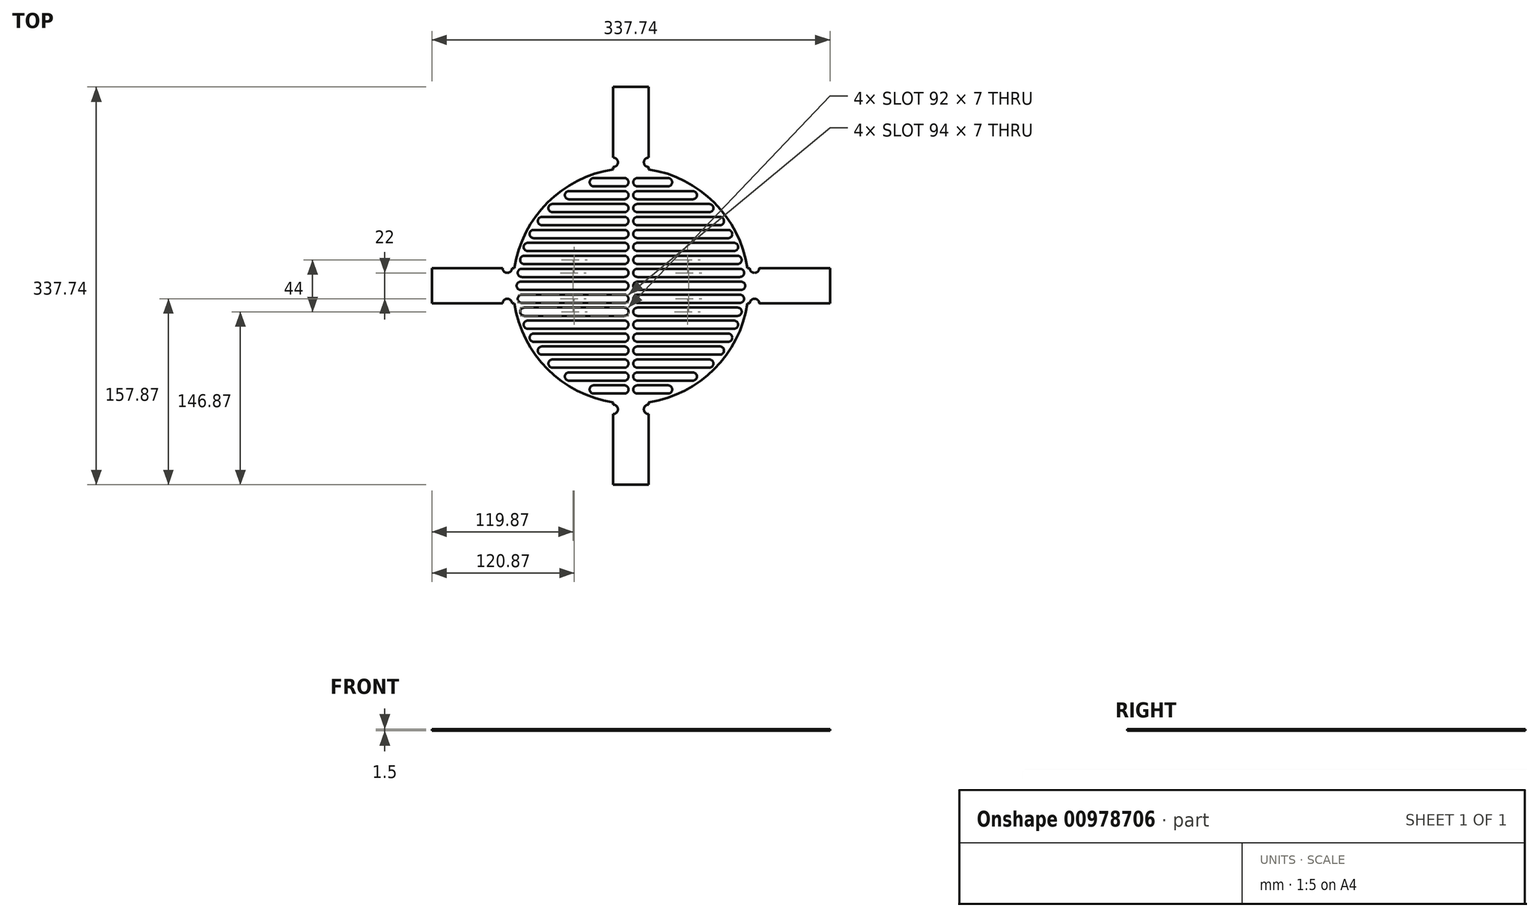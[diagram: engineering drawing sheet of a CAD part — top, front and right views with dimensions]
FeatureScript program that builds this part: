
annotation { "Feature Type Name" : "Feature", "Feature Type Description" : "" }
export const myFeature = defineFeature(function(context is Context, id is Id, definition is map)
    precondition{}
    {
        {
            var Q0;
            Q0=qCreatedBy(makeId("Top.planeOp"),FACE);
            var sketch = newSketch(context, id + "F0", { "sketchPlane" : qUnion([Q0])});
            skCircle(sketch, "E0", {"center": v(0, 0) * mm, "radius": 100 * mm});
            skSolve(sketch);
        }
        {
            var Q0;
            Q0 = qSketchRegion(id + "F0", true);
            extrude(context, id + "F1", {"entities" : qUnion([Q0]), "oppositeDirection" : true, "depth" : 1.5 * mm, "offsetDistance" : 25 * mm});
        }
        {
            var Q0;
            Q0=makeQuery(id+"F0.imprint","IMPRINT",FACE,{"disambiguationData":[TD([[makeQuery(id+"F0.imprint","IMPRINT",EDGE,{"derivedFrom":sQuery(id+"F0.wireOp",EDGE,"E0")}),1.0]])]});
            var sketch = newSketch(context, id + "F2", { "sketchPlane" : qUnion([Q0])});
            skLineSegment(sketch, "E1.bottom", {"start": v(-98.87, 15) * mm, "end": v(-168.87, 15) * mm});
            skLineSegment(sketch, "E1.top", {"start": v(-98.87, -15) * mm, "end": v(-168.87, -15) * mm});
            skLineSegment(sketch, "E1.left", {"start": v(-98.87, 15) * mm, "end": v(-98.87, -15) * mm});
            skLineSegment(sketch, "E1.right", {"start": v(-168.87, 15) * mm, "end": v(-168.87, -15) * mm});
            skLineSegment(sketch, "E2.bottom", {"start": v(98.87, 15) * mm, "end": v(168.87, 15) * mm});
            skLineSegment(sketch, "E2.top", {"start": v(98.87, -15) * mm, "end": v(168.87, -15) * mm});
            skLineSegment(sketch, "E2.left", {"start": v(98.87, 15) * mm, "end": v(98.87, -15) * mm});
            skLineSegment(sketch, "E2.right", {"start": v(168.87, 15) * mm, "end": v(168.87, -15) * mm});
            skLineSegment(sketch, "E3.bottom", {"start": v(-15, 98.87) * mm, "end": v(15, 98.87) * mm});
            skLineSegment(sketch, "E3.top", {"start": v(-15, 168.87) * mm, "end": v(15, 168.87) * mm});
            skLineSegment(sketch, "E3.left", {"start": v(-15, 98.87) * mm, "end": v(-15, 168.87) * mm});
            skLineSegment(sketch, "E3.right", {"start": v(15, 98.87) * mm, "end": v(15, 168.87) * mm});
            skLineSegment(sketch, "E4.bottom", {"start": v(-15, -98.87) * mm, "end": v(15, -98.87) * mm});
            skLineSegment(sketch, "E4.top", {"start": v(-15, -168.87) * mm, "end": v(15, -168.87) * mm});
            skLineSegment(sketch, "E4.left", {"start": v(-15, -98.87) * mm, "end": v(-15, -168.87) * mm});
            skLineSegment(sketch, "E4.right", {"start": v(15, -98.87) * mm, "end": v(15, -168.87) * mm});
            skSolve(sketch);
        }
        {
            var Q0;
            Q0 = qSketchRegion(id + "F2", true);
            extrude(context, id + "F3", {"entities" : qUnion([Q0]), "operationType" : NewBodyOperationType.ADD, "oppositeDirection" : true, "depth" : 1.5 * mm, "offsetDistance" : 25 * mm});
        }
        {
            var Q0;
            Q0=makeQuery(id+"F0.imprint","IMPRINT",FACE,{"disambiguationData":[TD([[makeQuery(id+"F0.imprint","IMPRINT",EDGE,{"derivedFrom":sQuery(id+"F0.wireOp",EDGE,"E0")}),1.0]])]});
            var sketch = newSketch(context, id + "F4", { "sketchPlane" : qUnion([Q0])});
            skLineSegment(sketch, "E5", {"start": v(-5.5, 0) * mm, "end": v(-93.5, 0) * mm});
            skArc(sketch, "E6.0.startCap", {"start": v(-5.5, 3.5) * mm, "mid": v(-2, 0) * mm, "end": v(-5.5, -3.5) * mm});
            skArc(sketch, "E6.0.endCap", {"start": v(-93.5, -3.5) * mm, "mid": v(-97, 0) * mm, "end": v(-93.5, 3.5) * mm});
            skLineSegment(sketch, "E6.0.left", {"start": v(-5.5, -3.5) * mm, "end": v(-93.5, -3.5) * mm});
            skLineSegment(sketch, "E6.0.right", {"start": v(-5.5, 3.5) * mm, "end": v(-93.5, 3.5) * mm});
            skLineSegment(sketch, "E7", {"start": v(-5.5, 11) * mm, "end": v(-92.5, 11) * mm});
            skArc(sketch, "E8.0.startCap", {"start": v(-5.5, 14.5) * mm, "mid": v(-2, 11) * mm, "end": v(-5.5, 7.5) * mm});
            skArc(sketch, "E8.0.endCap", {"start": v(-92.5, 7.5) * mm, "mid": v(-96, 11) * mm, "end": v(-92.5, 14.5) * mm});
            skLineSegment(sketch, "E8.0.left", {"start": v(-5.5, 7.5) * mm, "end": v(-92.5, 7.5) * mm});
            skLineSegment(sketch, "E8.0.right", {"start": v(-5.5, 14.5) * mm, "end": v(-92.5, 14.5) * mm});
            skLineSegment(sketch, "E9", {"start": v(-5.5, 22) * mm, "end": v(-90.5, 22) * mm});
            skArc(sketch, "E10.0.startCap", {"start": v(-5.5, 25.5) * mm, "mid": v(-2, 22) * mm, "end": v(-5.5, 18.5) * mm});
            skArc(sketch, "E10.0.endCap", {"start": v(-90.5, 18.5) * mm, "mid": v(-94, 22) * mm, "end": v(-90.5, 25.5) * mm});
            skLineSegment(sketch, "E10.0.left", {"start": v(-5.5, 18.5) * mm, "end": v(-90.5, 18.5) * mm});
            skLineSegment(sketch, "E10.0.right", {"start": v(-5.5, 25.5) * mm, "end": v(-90.5, 25.5) * mm});
            skLineSegment(sketch, "E11", {"start": v(-5.5, 44) * mm, "end": v(-82.5, 44) * mm});
            skArc(sketch, "E12.0.startCap", {"start": v(-5.5, 47.5) * mm, "mid": v(-2, 44) * mm, "end": v(-5.5, 40.5) * mm});
            skArc(sketch, "E12.0.endCap", {"start": v(-82.5, 40.5) * mm, "mid": v(-86, 44) * mm, "end": v(-82.5, 47.5) * mm});
            skLineSegment(sketch, "E12.0.left", {"start": v(-5.5, 40.5) * mm, "end": v(-82.5, 40.5) * mm});
            skLineSegment(sketch, "E12.0.right", {"start": v(-5.5, 47.5) * mm, "end": v(-82.5, 47.5) * mm});
            skLineSegment(sketch, "E13", {"start": v(-5.5, 33) * mm, "end": v(-87.5, 33) * mm});
            skArc(sketch, "E14.0.startCap", {"start": v(-5.5, 36.5) * mm, "mid": v(-2, 33) * mm, "end": v(-5.5, 29.5) * mm});
            skArc(sketch, "E14.0.endCap", {"start": v(-87.5, 29.5) * mm, "mid": v(-91, 33) * mm, "end": v(-87.5, 36.5) * mm});
            skLineSegment(sketch, "E14.0.left", {"start": v(-5.5, 29.5) * mm, "end": v(-87.5, 29.5) * mm});
            skLineSegment(sketch, "E14.0.right", {"start": v(-5.5, 36.5) * mm, "end": v(-87.5, 36.5) * mm});
            skLineSegment(sketch, "E15", {"start": v(-5.5, 55) * mm, "end": v(-75.5, 55) * mm});
            skArc(sketch, "E16.0.startCap", {"start": v(-5.5, 58.5) * mm, "mid": v(-2, 55) * mm, "end": v(-5.5, 51.5) * mm});
            skArc(sketch, "E16.0.endCap", {"start": v(-75.5, 51.5) * mm, "mid": v(-79, 55) * mm, "end": v(-75.5, 58.5) * mm});
            skLineSegment(sketch, "E16.0.left", {"start": v(-5.5, 51.5) * mm, "end": v(-75.5, 51.5) * mm});
            skLineSegment(sketch, "E16.0.right", {"start": v(-5.5, 58.5) * mm, "end": v(-75.5, 58.5) * mm});
            skLineSegment(sketch, "E17", {"start": v(-5.5, 66) * mm, "end": v(-66.5, 66) * mm});
            skArc(sketch, "E18.0.startCap", {"start": v(-5.5, 69.5) * mm, "mid": v(-2, 66) * mm, "end": v(-5.5, 62.5) * mm});
            skArc(sketch, "E18.0.endCap", {"start": v(-66.5, 62.5) * mm, "mid": v(-70, 66) * mm, "end": v(-66.5, 69.5) * mm});
            skLineSegment(sketch, "E18.0.left", {"start": v(-5.5, 62.5) * mm, "end": v(-66.5, 62.5) * mm});
            skLineSegment(sketch, "E18.0.right", {"start": v(-5.5, 69.5) * mm, "end": v(-66.5, 69.5) * mm});
            skLineSegment(sketch, "E19", {"start": v(-5.5, 77) * mm, "end": v(-52.5, 77) * mm});
            skArc(sketch, "E20.0.startCap", {"start": v(-5.5, 80.5) * mm, "mid": v(-2, 77) * mm, "end": v(-5.5, 73.5) * mm});
            skArc(sketch, "E20.0.endCap", {"start": v(-52.5, 73.5) * mm, "mid": v(-56, 77) * mm, "end": v(-52.5, 80.5) * mm});
            skLineSegment(sketch, "E20.0.left", {"start": v(-5.5, 73.5) * mm, "end": v(-52.5, 73.5) * mm});
            skLineSegment(sketch, "E20.0.right", {"start": v(-5.5, 80.5) * mm, "end": v(-52.5, 80.5) * mm});
            skLineSegment(sketch, "E21", {"start": v(-5.5, 88) * mm, "end": v(-31.5, 88) * mm});
            skArc(sketch, "E22.0.startCap", {"start": v(-5.5, 91.5) * mm, "mid": v(-2, 88) * mm, "end": v(-5.5, 84.5) * mm});
            skArc(sketch, "E22.0.endCap", {"start": v(-31.5, 84.5) * mm, "mid": v(-35, 88) * mm, "end": v(-31.5, 91.5) * mm});
            skLineSegment(sketch, "E22.0.left", {"start": v(-5.5, 84.5) * mm, "end": v(-31.5, 84.5) * mm});
            skLineSegment(sketch, "E22.0.right", {"start": v(-5.5, 91.5) * mm, "end": v(-31.5, 91.5) * mm});
            skArc(sketch, "E23.MirrorCS", {"start": v(-5.5, -3.5) * mm, "mid": v(-2, 0) * mm, "end": v(-5.5, 3.5) * mm});
            skArc(sketch, "E24.MirrorCS", {"start": v(-93.5, 3.5) * mm, "mid": v(-97, 0) * mm, "end": v(-93.5, -3.5) * mm});
            skLineSegment(sketch, "E25.MirrorCS", {"start": v(-5.5, -7.5) * mm, "end": v(-92.5, -7.5) * mm});
            skArc(sketch, "E26.MirrorCS", {"start": v(-90.5, -18.5) * mm, "mid": v(-94, -22) * mm, "end": v(-90.5, -25.5) * mm});
            skArc(sketch, "E27.MirrorCS", {"start": v(-75.5, -51.5) * mm, "mid": v(-79, -55) * mm, "end": v(-75.5, -58.5) * mm});
            skArc(sketch, "E28.MirrorCS", {"start": v(-87.5, -29.5) * mm, "mid": v(-91, -33) * mm, "end": v(-87.5, -36.5) * mm});
            skArc(sketch, "E29.MirrorCS", {"start": v(-31.5, -84.5) * mm, "mid": v(-35, -88) * mm, "end": v(-31.5, -91.5) * mm});
            skArc(sketch, "E30.MirrorCS", {"start": v(-5.5, -14.5) * mm, "mid": v(-2, -11) * mm, "end": v(-5.5, -7.5) * mm});
            skArc(sketch, "E31.MirrorCS", {"start": v(-5.5, -69.5) * mm, "mid": v(-2, -66) * mm, "end": v(-5.5, -62.5) * mm});
            skArc(sketch, "E32.MirrorCS", {"start": v(-5.5, -25.5) * mm, "mid": v(-2, -22) * mm, "end": v(-5.5, -18.5) * mm});
            skArc(sketch, "E33.MirrorCS", {"start": v(-5.5, -91.5) * mm, "mid": v(-2, -88) * mm, "end": v(-5.5, -84.5) * mm});
            skArc(sketch, "E34.MirrorCS", {"start": v(-52.5, -73.5) * mm, "mid": v(-56, -77) * mm, "end": v(-52.5, -80.5) * mm});
            skArc(sketch, "E35.MirrorCS", {"start": v(-66.5, -62.5) * mm, "mid": v(-70, -66) * mm, "end": v(-66.5, -69.5) * mm});
            skArc(sketch, "E36.MirrorCS", {"start": v(-5.5, -58.5) * mm, "mid": v(-2, -55) * mm, "end": v(-5.5, -51.5) * mm});
            skArc(sketch, "E37.MirrorCS", {"start": v(-5.5, -80.5) * mm, "mid": v(-2, -77) * mm, "end": v(-5.5, -73.5) * mm});
            skLineSegment(sketch, "E38.MirrorCS", {"start": v(-5.5, -80.5) * mm, "end": v(-52.5, -80.5) * mm});
            skLineSegment(sketch, "E39.MirrorCS", {"start": v(-5.5, -58.5) * mm, "end": v(-75.5, -58.5) * mm});
            skLineSegment(sketch, "E40.MirrorCS", {"start": v(-5.5, -73.5) * mm, "end": v(-52.5, -73.5) * mm});
            skLineSegment(sketch, "E41.MirrorCS", {"start": v(-5.5, -18.5) * mm, "end": v(-90.5, -18.5) * mm});
            skLineSegment(sketch, "E42.MirrorCS", {"start": v(-5.5, -69.5) * mm, "end": v(-66.5, -69.5) * mm});
            skLineSegment(sketch, "E43.MirrorCS", {"start": v(-5.5, -77) * mm, "end": v(-52.5, -77) * mm});
            skLineSegment(sketch, "E44.MirrorCS", {"start": v(-5.5, -33) * mm, "end": v(-87.5, -33) * mm});
            skArc(sketch, "E45.MirrorCS", {"start": v(-82.5, -40.5) * mm, "mid": v(-86, -44) * mm, "end": v(-82.5, -47.5) * mm});
            skArc(sketch, "E46.MirrorCS", {"start": v(-5.5, -47.5) * mm, "mid": v(-2, -44) * mm, "end": v(-5.5, -40.5) * mm});
            skLineSegment(sketch, "E47.MirrorCS", {"start": v(-5.5, -25.5) * mm, "end": v(-90.5, -25.5) * mm});
            skLineSegment(sketch, "E48.MirrorCS", {"start": v(-5.5, -14.5) * mm, "end": v(-92.5, -14.5) * mm});
            skLineSegment(sketch, "E49.MirrorCS", {"start": v(-5.5, -66) * mm, "end": v(-66.5, -66) * mm});
            skLineSegment(sketch, "E50.MirrorCS", {"start": v(-5.5, -36.5) * mm, "end": v(-87.5, -36.5) * mm});
            skArc(sketch, "E51.MirrorCS", {"start": v(-5.5, -36.5) * mm, "mid": v(-2, -33) * mm, "end": v(-5.5, -29.5) * mm});
            skLineSegment(sketch, "E52.MirrorCS", {"start": v(-5.5, -11) * mm, "end": v(-92.5, -11) * mm});
            skLineSegment(sketch, "E53.MirrorCS", {"start": v(-5.5, -40.5) * mm, "end": v(-82.5, -40.5) * mm});
            skLineSegment(sketch, "E54.MirrorCS", {"start": v(-5.5, -22) * mm, "end": v(-90.5, -22) * mm});
            skLineSegment(sketch, "E55.MirrorCS", {"start": v(-5.5, -62.5) * mm, "end": v(-66.5, -62.5) * mm});
            skLineSegment(sketch, "E56.MirrorCS", {"start": v(-5.5, -91.5) * mm, "end": v(-31.5, -91.5) * mm});
            skLineSegment(sketch, "E57.MirrorCS", {"start": v(-5.5, -51.5) * mm, "end": v(-75.5, -51.5) * mm});
            skLineSegment(sketch, "E58.MirrorCS", {"start": v(-5.5, -29.5) * mm, "end": v(-87.5, -29.5) * mm});
            skLineSegment(sketch, "E59.MirrorCS", {"start": v(-5.5, -88) * mm, "end": v(-31.5, -88) * mm});
            skArc(sketch, "E60.MirrorCS", {"start": v(-92.5, -7.5) * mm, "mid": v(-96, -11) * mm, "end": v(-92.5, -14.5) * mm});
            skLineSegment(sketch, "E61.MirrorCS", {"start": v(-5.5, -47.5) * mm, "end": v(-82.5, -47.5) * mm});
            skLineSegment(sketch, "E62.MirrorCS", {"start": v(-5.5, -84.5) * mm, "end": v(-31.5, -84.5) * mm});
            skLineSegment(sketch, "E63.MirrorCS", {"start": v(-5.5, -55) * mm, "end": v(-75.5, -55) * mm});
            skLineSegment(sketch, "E64.MirrorCS", {"start": v(-5.5, -44) * mm, "end": v(-82.5, -44) * mm});
            skArc(sketch, "E65.MirrorCS", {"start": v(5.5, -3.5) * mm, "mid": v(2, 0) * mm, "end": v(5.5, 3.5) * mm});
            skArc(sketch, "E66.MirrorCS", {"start": v(5.5, 3.5) * mm, "mid": v(2, 0) * mm, "end": v(5.5, -3.5) * mm});
            skArc(sketch, "E67.MirrorCS", {"start": v(93.5, 3.5) * mm, "mid": v(97, 0) * mm, "end": v(93.5, -3.5) * mm});
            skArc(sketch, "E68.MirrorCS", {"start": v(5.5, 47.5) * mm, "mid": v(2, 44) * mm, "end": v(5.5, 40.5) * mm});
            skArc(sketch, "E69.MirrorCS", {"start": v(5.5, 36.5) * mm, "mid": v(2, 33) * mm, "end": v(5.5, 29.5) * mm});
            skArc(sketch, "E70.MirrorCS", {"start": v(5.5, 58.5) * mm, "mid": v(2, 55) * mm, "end": v(5.5, 51.5) * mm});
            skArc(sketch, "E71.MirrorCS", {"start": v(5.5, -58.5) * mm, "mid": v(2, -55) * mm, "end": v(5.5, -51.5) * mm});
            skArc(sketch, "E72.MirrorCS", {"start": v(5.5, 25.5) * mm, "mid": v(2, 22) * mm, "end": v(5.5, 18.5) * mm});
            skArc(sketch, "E73.MirrorCS", {"start": v(5.5, 14.5) * mm, "mid": v(2, 11) * mm, "end": v(5.5, 7.5) * mm});
            skArc(sketch, "E74.MirrorCS", {"start": v(93.5, -3.5) * mm, "mid": v(97, 0) * mm, "end": v(93.5, 3.5) * mm});
            skArc(sketch, "E75.MirrorCS", {"start": v(5.5, -47.5) * mm, "mid": v(2, -44) * mm, "end": v(5.5, -40.5) * mm});
            skArc(sketch, "E76.MirrorCS", {"start": v(5.5, -69.5) * mm, "mid": v(2, -66) * mm, "end": v(5.5, -62.5) * mm});
            skArc(sketch, "E77.MirrorCS", {"start": v(5.5, -36.5) * mm, "mid": v(2, -33) * mm, "end": v(5.5, -29.5) * mm});
            skArc(sketch, "E78.MirrorCS", {"start": v(5.5, 69.5) * mm, "mid": v(2, 66) * mm, "end": v(5.5, 62.5) * mm});
            skArc(sketch, "E79.MirrorCS", {"start": v(5.5, -14.5) * mm, "mid": v(2, -11) * mm, "end": v(5.5, -7.5) * mm});
            skArc(sketch, "E80.MirrorCS", {"start": v(5.5, -25.5) * mm, "mid": v(2, -22) * mm, "end": v(5.5, -18.5) * mm});
            skArc(sketch, "E81.MirrorCS", {"start": v(5.5, 80.5) * mm, "mid": v(2, 77) * mm, "end": v(5.5, 73.5) * mm});
            skArc(sketch, "E82.MirrorCS", {"start": v(5.5, -80.5) * mm, "mid": v(2, -77) * mm, "end": v(5.5, -73.5) * mm});
            skArc(sketch, "E83.MirrorCS", {"start": v(92.5, 7.5) * mm, "mid": v(96, 11) * mm, "end": v(92.5, 14.5) * mm});
            skArc(sketch, "E84.MirrorCS", {"start": v(66.5, -62.5) * mm, "mid": v(70, -66) * mm, "end": v(66.5, -69.5) * mm});
            skArc(sketch, "E85.MirrorCS", {"start": v(92.5, -7.5) * mm, "mid": v(96, -11) * mm, "end": v(92.5, -14.5) * mm});
            skArc(sketch, "E86.MirrorCS", {"start": v(5.5, 91.5) * mm, "mid": v(2, 88) * mm, "end": v(5.5, 84.5) * mm});
            skArc(sketch, "E87.MirrorCS", {"start": v(82.5, -40.5) * mm, "mid": v(86, -44) * mm, "end": v(82.5, -47.5) * mm});
            skArc(sketch, "E88.MirrorCS", {"start": v(5.5, -91.5) * mm, "mid": v(2, -88) * mm, "end": v(5.5, -84.5) * mm});
            skArc(sketch, "E89.MirrorCS", {"start": v(52.5, 73.5) * mm, "mid": v(56, 77) * mm, "end": v(52.5, 80.5) * mm});
            skArc(sketch, "E90.MirrorCS", {"start": v(90.5, 18.5) * mm, "mid": v(94, 22) * mm, "end": v(90.5, 25.5) * mm});
            skArc(sketch, "E91.MirrorCS", {"start": v(75.5, 51.5) * mm, "mid": v(79, 55) * mm, "end": v(75.5, 58.5) * mm});
            skArc(sketch, "E92.MirrorCS", {"start": v(87.5, 29.5) * mm, "mid": v(91, 33) * mm, "end": v(87.5, 36.5) * mm});
            skArc(sketch, "E93.MirrorCS", {"start": v(31.5, 84.5) * mm, "mid": v(35, 88) * mm, "end": v(31.5, 91.5) * mm});
            skArc(sketch, "E94.MirrorCS", {"start": v(90.5, -18.5) * mm, "mid": v(94, -22) * mm, "end": v(90.5, -25.5) * mm});
            skArc(sketch, "E95.MirrorCS", {"start": v(87.5, -29.5) * mm, "mid": v(91, -33) * mm, "end": v(87.5, -36.5) * mm});
            skArc(sketch, "E96.MirrorCS", {"start": v(82.5, 40.5) * mm, "mid": v(86, 44) * mm, "end": v(82.5, 47.5) * mm});
            skArc(sketch, "E97.MirrorCS", {"start": v(66.5, 62.5) * mm, "mid": v(70, 66) * mm, "end": v(66.5, 69.5) * mm});
            skArc(sketch, "E98.MirrorCS", {"start": v(75.5, -51.5) * mm, "mid": v(79, -55) * mm, "end": v(75.5, -58.5) * mm});
            skArc(sketch, "E99.MirrorCS", {"start": v(31.5, -84.5) * mm, "mid": v(35, -88) * mm, "end": v(31.5, -91.5) * mm});
            skArc(sketch, "E100.MirrorCS", {"start": v(52.5, -73.5) * mm, "mid": v(56, -77) * mm, "end": v(52.5, -80.5) * mm});
            skLineSegment(sketch, "E101.MirrorCS", {"start": v(5.5, -88) * mm, "end": v(31.5, -88) * mm});
            skLineSegment(sketch, "E102.MirrorCS", {"start": v(5.5, 0) * mm, "end": v(93.5, 0) * mm});
            skLineSegment(sketch, "E103.MirrorCS", {"start": v(5.5, 73.5) * mm, "end": v(52.5, 73.5) * mm});
            skLineSegment(sketch, "E104.MirrorCS", {"start": v(5.5, 7.5) * mm, "end": v(92.5, 7.5) * mm});
            skLineSegment(sketch, "E105.MirrorCS", {"start": v(5.5, -58.5) * mm, "end": v(75.5, -58.5) * mm});
            skLineSegment(sketch, "E106.MirrorCS", {"start": v(5.5, 40.5) * mm, "end": v(82.5, 40.5) * mm});
            skLineSegment(sketch, "E107.MirrorCS", {"start": v(5.5, 62.5) * mm, "end": v(66.5, 62.5) * mm});
            skLineSegment(sketch, "E108.MirrorCS", {"start": v(5.5, -11) * mm, "end": v(92.5, -11) * mm});
            skLineSegment(sketch, "E109.MirrorCS", {"start": v(5.5, 29.5) * mm, "end": v(87.5, 29.5) * mm});
            skLineSegment(sketch, "E110.MirrorCS", {"start": v(5.5, 11) * mm, "end": v(92.5, 11) * mm});
            skLineSegment(sketch, "E111.MirrorCS", {"start": v(5.5, 3.5) * mm, "end": v(93.5, 3.5) * mm});
            skLineSegment(sketch, "E112.MirrorCS", {"start": v(5.5, -14.5) * mm, "end": v(92.5, -14.5) * mm});
            skLineSegment(sketch, "E113.MirrorCS", {"start": v(5.5, -77) * mm, "end": v(52.5, -77) * mm});
            skLineSegment(sketch, "E114.MirrorCS", {"start": v(5.5, 55) * mm, "end": v(75.5, 55) * mm});
            skLineSegment(sketch, "E115.MirrorCS", {"start": v(5.5, -3.5) * mm, "end": v(93.5, -3.5) * mm});
            skLineSegment(sketch, "E116.MirrorCS", {"start": v(5.5, -33) * mm, "end": v(87.5, -33) * mm});
            skLineSegment(sketch, "E117.MirrorCS", {"start": v(5.5, 91.5) * mm, "end": v(31.5, 91.5) * mm});
            skLineSegment(sketch, "E118.MirrorCS", {"start": v(5.5, -51.5) * mm, "end": v(75.5, -51.5) * mm});
            skLineSegment(sketch, "E119.MirrorCS", {"start": v(5.5, -25.5) * mm, "end": v(90.5, -25.5) * mm});
            skLineSegment(sketch, "E120.MirrorCS", {"start": v(5.5, 69.5) * mm, "end": v(66.5, 69.5) * mm});
            skLineSegment(sketch, "E121.MirrorCS", {"start": v(5.5, 66) * mm, "end": v(66.5, 66) * mm});
            skLineSegment(sketch, "E122.MirrorCS", {"start": v(5.5, 77) * mm, "end": v(52.5, 77) * mm});
            skLineSegment(sketch, "E123.MirrorCS", {"start": v(5.5, -44) * mm, "end": v(82.5, -44) * mm});
            skLineSegment(sketch, "E124.MirrorCS", {"start": v(5.5, 58.5) * mm, "end": v(75.5, 58.5) * mm});
            skLineSegment(sketch, "E125.MirrorCS", {"start": v(5.5, -18.5) * mm, "end": v(90.5, -18.5) * mm});
            skLineSegment(sketch, "E126.MirrorCS", {"start": v(5.5, 51.5) * mm, "end": v(75.5, 51.5) * mm});
            skLineSegment(sketch, "E127.MirrorCS", {"start": v(5.5, 14.5) * mm, "end": v(92.5, 14.5) * mm});
            skLineSegment(sketch, "E128.MirrorCS", {"start": v(5.5, -47.5) * mm, "end": v(82.5, -47.5) * mm});
            skLineSegment(sketch, "E129.MirrorCS", {"start": v(5.5, -7.5) * mm, "end": v(92.5, -7.5) * mm});
            skLineSegment(sketch, "E130.MirrorCS", {"start": v(5.5, 33) * mm, "end": v(87.5, 33) * mm});
            skLineSegment(sketch, "E131.MirrorCS", {"start": v(5.5, -84.5) * mm, "end": v(31.5, -84.5) * mm});
            skLineSegment(sketch, "E132.MirrorCS", {"start": v(5.5, 88) * mm, "end": v(31.5, 88) * mm});
            skLineSegment(sketch, "E133.MirrorCS", {"start": v(5.5, 44) * mm, "end": v(82.5, 44) * mm});
            skLineSegment(sketch, "E134.MirrorCS", {"start": v(5.5, -91.5) * mm, "end": v(31.5, -91.5) * mm});
            skLineSegment(sketch, "E135.MirrorCS", {"start": v(5.5, -40.5) * mm, "end": v(82.5, -40.5) * mm});
            skLineSegment(sketch, "E136.MirrorCS", {"start": v(5.5, -73.5) * mm, "end": v(52.5, -73.5) * mm});
            skLineSegment(sketch, "E137.MirrorCS", {"start": v(5.5, -62.5) * mm, "end": v(66.5, -62.5) * mm});
            skLineSegment(sketch, "E138.MirrorCS", {"start": v(5.5, -80.5) * mm, "end": v(52.5, -80.5) * mm});
            skLineSegment(sketch, "E139.MirrorCS", {"start": v(5.5, 18.5) * mm, "end": v(90.5, 18.5) * mm});
            skLineSegment(sketch, "E140.MirrorCS", {"start": v(5.5, -55) * mm, "end": v(75.5, -55) * mm});
            skLineSegment(sketch, "E141.MirrorCS", {"start": v(5.5, 47.5) * mm, "end": v(82.5, 47.5) * mm});
            skLineSegment(sketch, "E142.MirrorCS", {"start": v(5.5, -22) * mm, "end": v(90.5, -22) * mm});
            skLineSegment(sketch, "E143.MirrorCS", {"start": v(5.5, -66) * mm, "end": v(66.5, -66) * mm});
            skLineSegment(sketch, "E144.MirrorCS", {"start": v(5.5, 80.5) * mm, "end": v(52.5, 80.5) * mm});
            skLineSegment(sketch, "E145.MirrorCS", {"start": v(5.5, 22) * mm, "end": v(90.5, 22) * mm});
            skLineSegment(sketch, "E146.MirrorCS", {"start": v(5.5, -69.5) * mm, "end": v(66.5, -69.5) * mm});
            skLineSegment(sketch, "E147.MirrorCS", {"start": v(5.5, 84.5) * mm, "end": v(31.5, 84.5) * mm});
            skLineSegment(sketch, "E148.MirrorCS", {"start": v(5.5, -29.5) * mm, "end": v(87.5, -29.5) * mm});
            skLineSegment(sketch, "E149.MirrorCS", {"start": v(5.5, 25.5) * mm, "end": v(90.5, 25.5) * mm});
            skLineSegment(sketch, "E150.MirrorCS", {"start": v(5.5, -36.5) * mm, "end": v(87.5, -36.5) * mm});
            skLineSegment(sketch, "E151.MirrorCS", {"start": v(5.5, 36.5) * mm, "end": v(87.5, 36.5) * mm});
            skSolve(sketch);
        }
        {
            var Q0;
            Q0 = qSketchRegion(id + "F4", true);
            extrude(context, id + "F5", {"entities" : qUnion([Q0]), "operationType" : NewBodyOperationType.REMOVE, "oppositeDirection" : true, "depth" : 25 * mm, "offsetDistance" : 25 * mm, "hasSecondDirection" : true, "secondDirectionOppositeDirection" : false, "secondDirectionDepth" : 25 * mm});
        }
        {
            var Q0;
            Q0=makeQuery(id+"F3.boolean.opBoolean","MERGE",FACE,{"derivedFrom":[makeQuery(id+"F1.opExtrude","CAP_FACE",FACE,{"disambiguationData":[OSD([sQuery(id+"F0.wireOp",EDGE,"E0")])],"isStart":true}),makeQuery(id+"F3.opExtrude","CAP_FACE",FACE,{"disambiguationData":[OSD([sQuery(id+"F2.wireOp",EDGE,"E1.bottom"),sQuery(id+"F2.wireOp",EDGE,"E1.top"),sQuery(id+"F2.wireOp",EDGE,"E1.left"),sQuery(id+"F2.wireOp",EDGE,"E1.right")])],"isStart":true}),makeQuery(id+"F3.opExtrude","CAP_FACE",FACE,{"disambiguationData":[OSD([sQuery(id+"F2.wireOp",EDGE,"E2.bottom"),sQuery(id+"F2.wireOp",EDGE,"E2.top"),sQuery(id+"F2.wireOp",EDGE,"E2.left"),sQuery(id+"F2.wireOp",EDGE,"E2.right")])],"isStart":true}),makeQuery(id+"F3.opExtrude","CAP_FACE",FACE,{"disambiguationData":[OSD([sQuery(id+"F2.wireOp",EDGE,"E3.bottom"),sQuery(id+"F2.wireOp",EDGE,"E3.top"),sQuery(id+"F2.wireOp",EDGE,"E3.left"),sQuery(id+"F2.wireOp",EDGE,"E3.right")])],"isStart":true}),makeQuery(id+"F3.opExtrude","CAP_FACE",FACE,{"disambiguationData":[OSD([sQuery(id+"F2.wireOp",EDGE,"E4.bottom"),sQuery(id+"F2.wireOp",EDGE,"E4.top"),sQuery(id+"F2.wireOp",EDGE,"E4.left"),sQuery(id+"F2.wireOp",EDGE,"E4.right")])],"isStart":true})]});
            var sketch = newSketch(context, id + "F6", { "sketchPlane" : qUnion([Q0])});
            skCircle(sketch, "E152", {"center": v(15, 104.87) * mm, "radius": 4 * mm});
            skCircle(sketch, "E153.MirrorC", {"center": v(-15, 104.87) * mm, "radius": 4 * mm});
            skCircle(sketch, "E154.1.0", {"center": v(-104.87, 15) * mm, "radius": 4 * mm});
            skCircle(sketch, "E154.1.1", {"center": v(-104.87, -15) * mm, "radius": 4 * mm});
            skCircle(sketch, "E154.2.0", {"center": v(-15, -104.87) * mm, "radius": 4 * mm});
            skCircle(sketch, "E154.2.1", {"center": v(15, -104.87) * mm, "radius": 4 * mm});
            skCircle(sketch, "E154.3.0", {"center": v(104.87, -15) * mm, "radius": 4 * mm});
            skCircle(sketch, "E154.3.1", {"center": v(104.87, 15) * mm, "radius": 4 * mm});
            skPoint(sketch, "E154.center", {"position": v(0, 0) * mm});
            skSolve(sketch);
        }
        {
            var Q0;
            Q0 = qSketchRegion(id + "F6", true);
            extrude(context, id + "F7", {"entities" : qUnion([Q0]), "operationType" : NewBodyOperationType.REMOVE, "depth" : 25 * mm, "offsetDistance" : 25 * mm, "hasSecondDirection" : true, "secondDirectionOppositeDirection" : true, "secondDirectionDepth" : 25 * mm});
        }
    });
